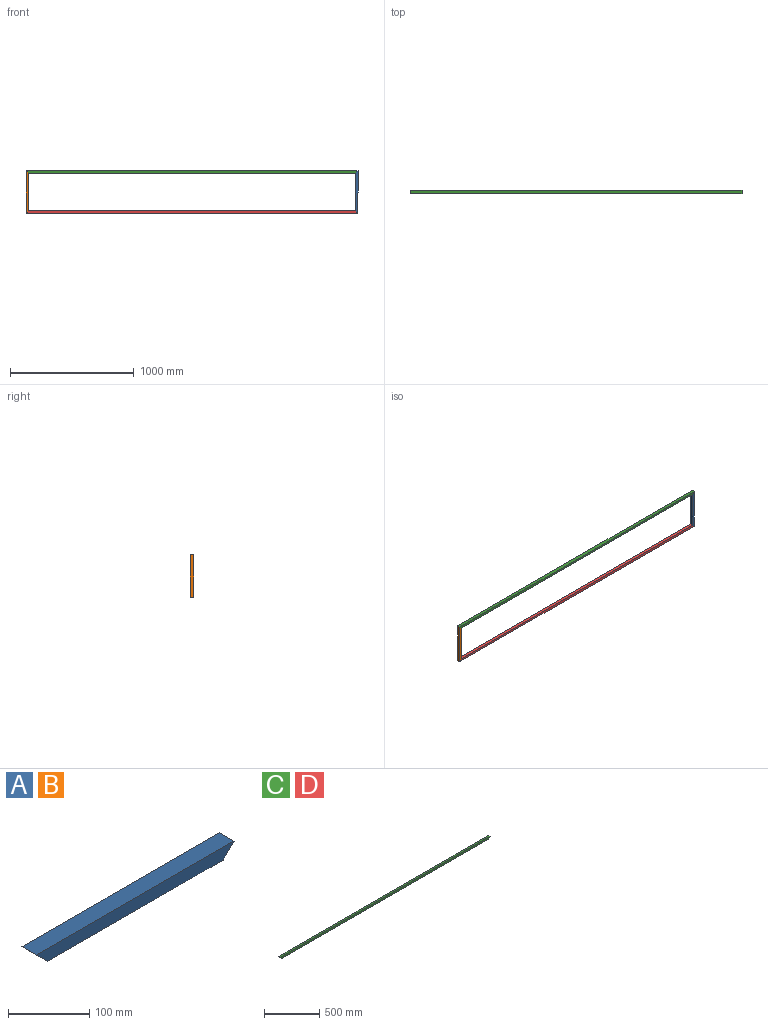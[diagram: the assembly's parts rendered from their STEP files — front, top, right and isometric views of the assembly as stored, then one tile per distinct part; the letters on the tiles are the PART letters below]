
ASSEMBLY  parts=4 mates=6
PART A: 6 faces, bbox 342.9x25.4x19.1 mm
  f0: plane 342.9x19.05mm, normal (0,-1,0), area 6169.3mm2, adj f1,f3,f4,f5
  f1: plane 304.8x25.4mm, normal (0,0,-1), area 7741.9mm2, adj f0,f2,f4,f5
  f2: plane 342.9x19.05mm, normal (0,1,0), area 6169.3mm2, adj f1,f3,f4,f5
  f3: plane 342.9x25.4mm, normal (0,0,1), area 8709.7mm2, adj f0,f2,f4,f5
  f4: plane 25.4x19.05mm, normal (-0.71,0,-0.71), area 684.3mm2, adj f0,f1,f2,f3
  f5: plane 25.4x19.05mm, normal (0.71,0,-0.71), area 684.3mm2, adj f0,f1,f2,f3
PART B: same geometry as A
PART C: 6 faces, bbox 2686.1x25.4x19.1 mm
  f0: plane 2686.05x19.05mm, normal (0,-1,0), area 50806.3mm2, adj f1,f3,f4,f5
  f1: plane 2647.95x25.4mm, normal (0,0,-1), area 67257.9mm2, adj f0,f2,f4,f5
  f2: plane 2686.05x19.05mm, normal (0,1,0), area 50806.3mm2, adj f1,f3,f4,f5
  f3: plane 2686.05x25.4mm, normal (0,0,1), area 68225.7mm2, adj f0,f2,f4,f5
  f4: plane 25.4x19.05mm, normal (-0.71,0,-0.71), area 684.3mm2, adj f0,f1,f2,f3
  f5: plane 25.4x19.05mm, normal (0.71,0,-0.71), area 684.3mm2, adj f0,f1,f2,f3
PART D: same geometry as C
PLACE A rot(axis=(0.71,0,0.71),180deg) t=(68.46,116.64,-292.31)mm
PLACE B rot(axis=(0.71,0,-0.71),180deg) t=(-2579.49,116.64,50.59)mm
PLACE C rot(axis=(0,0,1),180deg) t=(87.51,116.64,31.54)mm
PLACE D rot(axis=(1,0,0),180deg) t=(-2598.54,116.64,-273.26)mm
MATE planar B.f0 <-> A.f0  axis (0,1,0) through (-2589.2,116.64,-120.86)mm
MATE fastened B.f5 <-> D.f4  axis (0.71,0,-0.71) through (-2589.02,103.94,-282.79)mm
MATE planar D.f0 <-> C.f0  axis (0,1,0) through (-1255.52,116.64,-282.81)mm
MATE fastened D.f5 <-> A.f4  axis (0.71,0,0.71) through (77.98,103.94,-282.79)mm
MATE fastened C.f4 <-> A.f5  axis (0.71,0,-0.71) through (77.98,103.94,41.06)mm
MATE planar B.f0 <-> C.f0  axis (0,1,0) through (-2589.2,116.64,-120.86)mm
